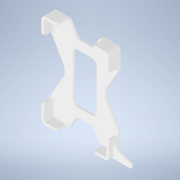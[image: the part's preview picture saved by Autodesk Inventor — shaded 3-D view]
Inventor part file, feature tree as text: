
AUTODESK INVENTOR PART (.ipt)
format: ipt  version: 2020 (Build 240168000, 168)  size: 785,408 bytes
history: native  units: mm
features: fillet x10, extrude x5, sketch x5, projected_geometry x4, mirror x2, plane x2
ambient origin geometry x8: Origin, YZ Plane, XZ Plane, XY Plane, X Axis, Y Axis, Z Axis, Center Point
bodies: Solid1 (feature_tree)
feature tree (28):
  extrude  "Extrusion1"  Depth=106.0mm
  extrude  "Extrusion2"  Depth=3.0mm
  extrude  "Extrusion3"  Depth=20.0mm
  mirror  "Mirror1"
  mirror  "Mirror2"
  plane  "Work Plane1"
  extrude  "Extrusion4"  Depth=15.0mm
  extrude  "Extrusion5"  Depth=30.0mm
  fillet  "Fillet1"  Radius=15.0mm
  fillet  "Fillet2"  Radius=17.5mm
  fillet  "Fillet3"  Radius=11.0mm
  fillet  "Fillet4"  Radius=20.0mm
  fillet  "Fillet5"  Radius=5.0mm
  fillet  "Fillet6"  Radius=3.0mm
  fillet  "Fillet7"  Radius=10.0mm
  fillet  "Fillet8"  Radius=2.0mm
  fillet  "Fillet9"  Radius=5.0mm
  fillet  "Fillet10"  Radius=3.0mm
  plane  "Work Plane2"
  sketch  "Sketch1"  dims[d0=76.0mm d1=106.0mm]
  sketch  "Sketch2"  dims[d2=3.0mm d3=0.0mm d4=3.0mm]
  projected_geometry  "Projected Loop1"
  sketch  "Sketch3"  dims[d5=17.5mm d6=20.0mm]
  projected_geometry  "Projected Loop2"
  sketch  "Sketch4"  dims[d7=11.0mm d8=0.0mm d9=15.0mm]
  projected_geometry  "Projected Loop3"
  sketch  "Sketch5"  dims[d10=30.0deg d11=30.0mm d12=15.0mm d13=17.5mm d14=11.0mm d15=0.0mm d16=20.0mm d17=5.0mm d18=3.0mm d19=0.0mm d20=10.0mm d21=2.0mm d22=5.0mm d23=3.0mm d24=5.0mm d25=2.0mm d26=2.0mm d27=0.5mm d28=1.0mm d29=1.0mm d30=12.217305mm d31=10.0mm d32=10.0mm d33=0.0mm d34=0.0mm]
  projected_geometry  "Projected Loop4"
